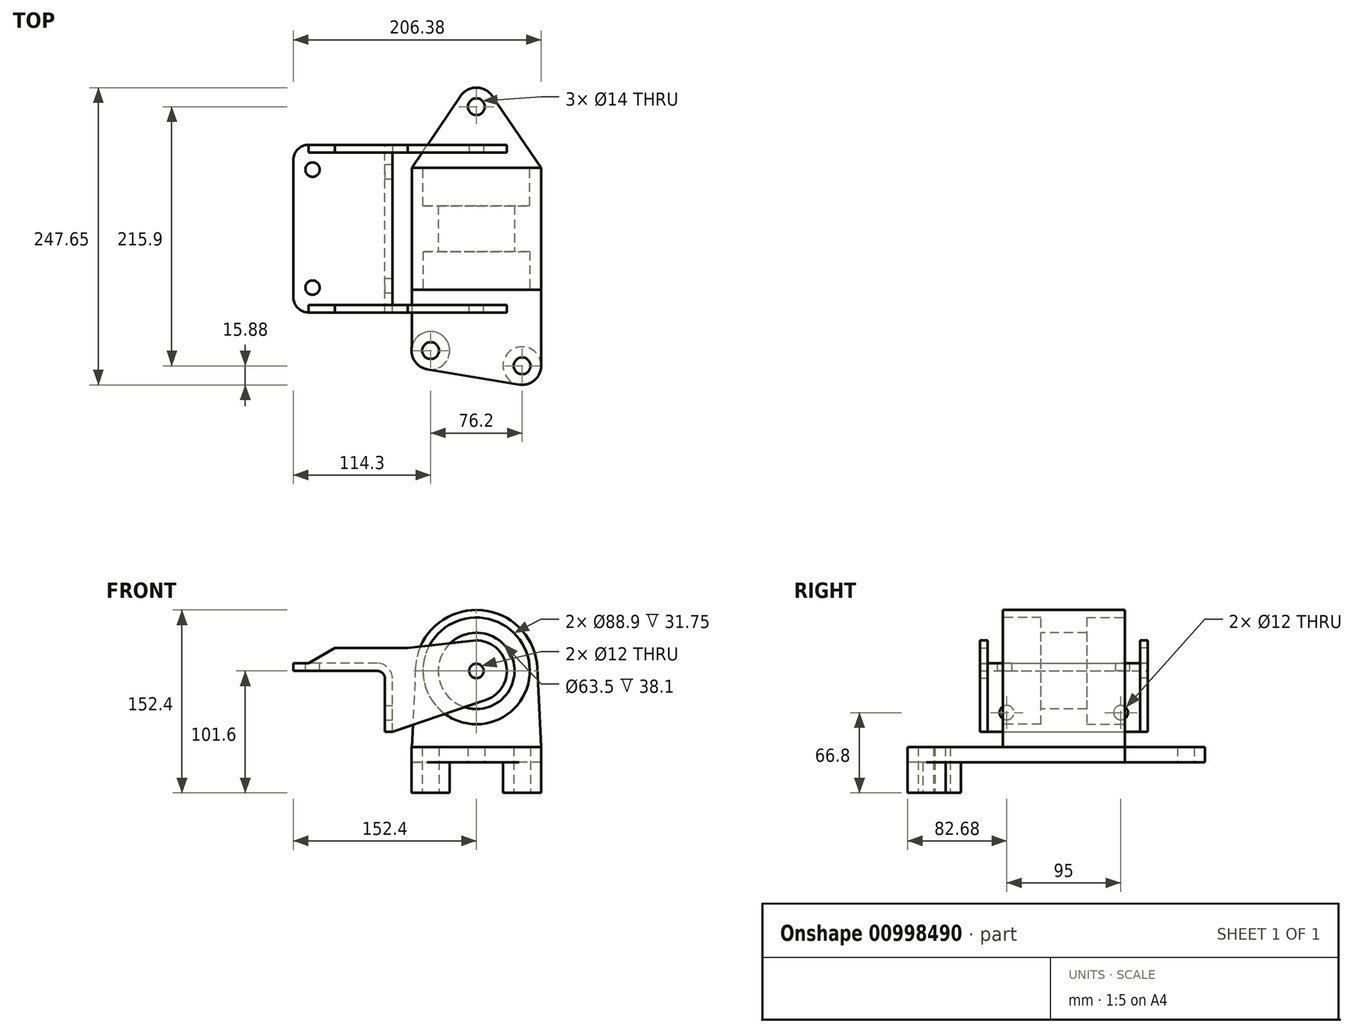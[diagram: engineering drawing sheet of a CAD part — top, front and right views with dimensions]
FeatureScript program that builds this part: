
annotation { "Feature Type Name" : "Feature", "Feature Type Description" : "" }
export const myFeature = defineFeature(function(context is Context, id is Id, definition is map)
    precondition{}
    {
        {
            var Q0;
            Q0=qCreatedBy(makeId("Top.planeOp"),FACE);
            var sketch = newSketch(context, id + "F0", { "sketchPlane" : qUnion([Q0])});
            skLineSegment(sketch, "E0", {"start": v(-38.1, -203.2) * mm, "end": v(0, 0) * mm});
            skLineSegment(sketch, "E1", {"start": v(0, 0) * mm, "end": v(38.1, -215.9) * mm});
            skSolve(sketch);
        }
        {
            var Q0;
            Q0=qCreatedBy(makeId("Top.planeOp"),FACE);
            var sketch = newSketch(context, id + "F1", { "sketchPlane" : qUnion([Q0])});
            skLineSegment(sketch, "E2.0", {"start": v(15.63, 2.76) * mm, "end": v(53.73, -213.14) * mm});
            skLineSegment(sketch, "E2.1", {"start": v(-53.7, -200.27) * mm, "end": v(-15.6, 2.93) * mm});
            skPoint(sketch, "E3.visualSharp", {"position": v(0.47, 88.67) * mm});
            skArc(sketch, "E3.filletArc", {"start": v(15.63, 2.76) * mm, "mid": v(0.08, 15.87) * mm, "end": v(-15.6, 2.93) * mm});
            skLineSegment(sketch, "E4", {"start": v(-53.7, -200.27) * mm, "end": v(-38.1, -203.2) * mm, "construction": true});
            skLineSegment(sketch, "E5", {"start": v(53.73, -213.14) * mm, "end": v(38.1, -215.9) * mm, "construction": true});
            skArc(sketch, "E6", {"start": v(-53.7, -200.27) * mm, "mid": v(-51.11, -212.3) * mm, "end": v(-40.7, -218.86) * mm});
            skPoint(sketch, "E6.endSnap0", {"position": v(-45.9, -201.74) * mm});
            skLineSegment(sketch, "E7", {"start": v(-40.7, -218.86) * mm, "end": v(35.5, -231.56) * mm});
            skArc(sketch, "E8", {"start": v(35.5, -231.56) * mm, "mid": v(49.38, -227.07) * mm, "end": v(53.73, -213.14) * mm});
            skCircle(sketch, "E9", {"center": v(0, 0) * mm, "radius": 7 * mm});
            skCircle(sketch, "E10", {"center": v(-38.1, -203.2) * mm, "radius": 7 * mm});
            skCircle(sketch, "E11", {"center": v(38.1, -215.9) * mm, "radius": 7 * mm});
            skSolve(sketch);
        }
        {
            var Q0;
            Q0 = qSketchRegion(id + "F1", true);
            extrude(context, id + "F2", {"entities" : qUnion([Q0]), "depth" : 12.7 * mm, "offsetDistance" : 25.4 * mm});
        }
        {
            var Q0;
            Q0=makeQuery(id+"F2.opExtrude","CAP_FACE",FACE,{"disambiguationData":[OSD([sQuery(id+"F1.wireOp",EDGE,"E2.0"),sQuery(id+"F1.wireOp",EDGE,"E2.1"),sQuery(id+"F1.wireOp",EDGE,"E3.filletArc"),sQuery(id+"F1.wireOp",EDGE,"E6"),sQuery(id+"F1.wireOp",EDGE,"E7"),sQuery(id+"F1.wireOp",EDGE,"E8"),sQuery(id+"F1.wireOp",EDGE,"E9"),sQuery(id+"F1.wireOp",EDGE,"E10"),sQuery(id+"F1.wireOp",EDGE,"E11")])],"isStart":true});
            var sketch = newSketch(context, id + "F3", { "sketchPlane" : qUnion([Q0])});
            skCircle(sketch, "E12", {"center": v(-38.1, 203.2) * mm, "radius": 15.87 * mm});
            skCircle(sketch, "E13.0", {"center": v(-38.1, 203.2) * mm, "radius": 7 * mm});
            skSolve(sketch);
        }
        {
            var Q0;
            Q0 = qSketchRegion(id + "F3", true);
            extrude(context, id + "F4", {"entities" : qUnion([Q0]), "operationType" : NewBodyOperationType.ADD, "depth" : 25.4 * mm, "offsetDistance" : 25.4 * mm});
        }
        {
            var Q0;
            Q0=makeQuery(id+"F2.opExtrude","CAP_FACE",FACE,{"disambiguationData":[OSD([sQuery(id+"F1.wireOp",EDGE,"E2.0"),sQuery(id+"F1.wireOp",EDGE,"E2.1"),sQuery(id+"F1.wireOp",EDGE,"E3.filletArc"),sQuery(id+"F1.wireOp",EDGE,"E6"),sQuery(id+"F1.wireOp",EDGE,"E7"),sQuery(id+"F1.wireOp",EDGE,"E8"),sQuery(id+"F1.wireOp",EDGE,"E9"),sQuery(id+"F1.wireOp",EDGE,"E10"),sQuery(id+"F1.wireOp",EDGE,"E11")])],"isStart":true});
            var sketch = newSketch(context, id + "F5", { "sketchPlane" : qUnion([Q0])});
            skCircle(sketch, "E14", {"center": v(38.1, 215.9) * mm, "radius": 15.88 * mm});
            skCircle(sketch, "E15.0", {"center": v(38.1, 215.9) * mm, "radius": 7 * mm});
            skSolve(sketch);
        }
        {
            var Q0;
            Q0 = qSketchRegion(id + "F5", true);
            extrude(context, id + "F6", {"entities" : qUnion([Q0]), "operationType" : NewBodyOperationType.ADD, "depth" : 25.4 * mm, "offsetDistance" : 25.4 * mm});
        }
        {
            var Q0;
            Q0=qCreatedBy(makeId("Front.planeOp"),FACE);
            cPlane(context, id + "F7", {"entities" : qUnion([Q0]), "cplaneType" : CPlaneType.OFFSET, "offset" : 101.6 * mm, "width" : 152.4 * mm, "height" : 152.4 * mm});
        }
        {
            var Q0;
            Q0=qCreatedBy(id+"F7.planeOp",FACE);
            var sketch = newSketch(context, id + "F8", { "sketchPlane" : qUnion([Q0])});
            skLineSegment(sketch, "E16.0.0", {"start": v(-53.98, 12.7) * mm, "end": v(-40.7, 12.7) * mm, "construction": true});
            skLineSegment(sketch, "E16.0.1", {"start": v(-40.7, 12.7) * mm, "end": v(35.5, 12.7) * mm, "construction": true});
            skLineSegment(sketch, "E16.0.2", {"start": v(35.5, 12.7) * mm, "end": v(53.97, 12.7) * mm, "construction": true});
            skLineSegment(sketch, "E16.0.3", {"start": v(53.73, 12.7) * mm, "end": v(15.63, 12.7) * mm, "construction": true});
            skLineSegment(sketch, "E16.0.4", {"start": v(15.63, 12.7) * mm, "end": v(-15.6, 12.7) * mm, "construction": true});
            skLineSegment(sketch, "E16.0.5", {"start": v(-15.6, 12.7) * mm, "end": v(-53.7, 12.7) * mm, "construction": true});
            skArc(sketch, "E17", {"start": v(50.74, 78.69) * mm, "mid": v(-0.1, 127) * mm, "end": v(-50.75, 78.48) * mm});
            skLineSegment(sketch, "E18", {"start": v(50.74, 78.69) * mm, "end": v(53.98, 12.7) * mm});
            skLineSegment(sketch, "E19", {"start": v(-50.75, 78.48) * mm, "end": v(-53.7, 12.7) * mm});
            skLineSegment(sketch, "E20", {"start": v(-53.7, 12.7) * mm, "end": v(53.97, 12.7) * mm});
            skSolve(sketch);
        }
        {
            var Q0;
            Q0 = qSketchRegion(id + "F8", true);
            extrude(context, id + "F9", {"entities" : qUnion([Q0]), "operationType" : NewBodyOperationType.ADD, "endBound" : BoundingType.SYMMETRIC, "depth" : 101.6 * mm, "offsetDistance" : 25.4 * mm});
        }
        {
            var Q0;
            Q0=makeQuery(id+"F9.opExtrude","CAP_FACE",FACE,{"disambiguationData":[OSD([sQuery(id+"F8.wireOp",EDGE,"E17"),sQuery(id+"F8.wireOp",EDGE,"E18"),sQuery(id+"F8.wireOp",EDGE,"E19"),sQuery(id+"F8.wireOp",EDGE,"E20")])],"isStart":false});
            var sketch = newSketch(context, id + "F10", { "sketchPlane" : qUnion([Q0])});
            skCircle(sketch, "E21", {"center": v(0, 76.2) * mm, "radius": 44.45 * mm});
            skSolve(sketch);
        }
        {
            var Q0;
            Q0 = qSketchRegion(id + "F10", true);
            extrude(context, id + "F11", {"entities" : qUnion([Q0]), "operationType" : NewBodyOperationType.REMOVE, "oppositeDirection" : true, "depth" : 31.75 * mm, "offsetDistance" : 25.4 * mm});
        }
        {
            var Q0;
            Q0=makeQuery(id+"F9.opExtrude","CAP_FACE",FACE,{"disambiguationData":[OSD([sQuery(id+"F8.wireOp",EDGE,"E17"),sQuery(id+"F8.wireOp",EDGE,"E18"),sQuery(id+"F8.wireOp",EDGE,"E19"),sQuery(id+"F8.wireOp",EDGE,"E20")])],"isStart":true});
            var sketch = newSketch(context, id + "F12", { "sketchPlane" : qUnion([Q0])});
            skCircle(sketch, "E22.0", {"center": v(0, 76.2) * mm, "radius": 44.45 * mm});
            skSolve(sketch);
        }
        {
            var Q0;
            Q0 = qSketchRegion(id + "F12", true);
            extrude(context, id + "F13", {"entities" : qUnion([Q0]), "operationType" : NewBodyOperationType.REMOVE, "oppositeDirection" : true, "depth" : 31.75 * mm, "offsetDistance" : 25.4 * mm});
        }
        {
            var Q0;
            Q0=makeQuery(id+"F11.boolean.opBoolean","COPY",FACE,{"derivedFrom":makeQuery(id+"F11.opExtrude","CAP_FACE",FACE,{"disambiguationData":[OSD([sQuery(id+"F10.wireOp",EDGE,"E21")])],"isStart":false})});
            var sketch = newSketch(context, id + "F14", { "sketchPlane" : qUnion([Q0])});
            skCircle(sketch, "E23", {"center": v(0, 76.2) * mm, "radius": 31.75 * mm});
            skSolve(sketch);
        }
        {
            var Q0;
            Q0 = qSketchRegion(id + "F14", true);
            extrude(context, id + "F15", {"entities" : qUnion([Q0]), "operationType" : NewBodyOperationType.REMOVE, "endBound" : BoundingType.THROUGH_ALL, "oppositeDirection" : true, "depth" : 25.4 * mm, "offsetDistance" : 25.4 * mm});
        }
        {
            var Q0;
            Q0=qCreatedBy(makeId("Front.planeOp"),FACE);
            var sketch = newSketch(context, id + "F16", { "sketchPlane" : qUnion([Q0])});
            skLineSegment(sketch, "E24", {"start": v(-76.2, 25.4) * mm, "end": v(-76.2, 76.2) * mm});
            skLineSegment(sketch, "E25", {"start": v(-76.2, 76.2) * mm, "end": v(-152.4, 76.2) * mm});
            skLineSegment(sketch, "E26.0", {"start": v(-69.85, 82.55) * mm, "end": v(-152.4, 82.55) * mm});
            skLineSegment(sketch, "E26.1", {"start": v(-69.85, 25.4) * mm, "end": v(-69.85, 82.55) * mm});
            skLineSegment(sketch, "E27", {"start": v(-152.4, 76.2) * mm, "end": v(-152.4, 82.55) * mm});
            skLineSegment(sketch, "E28", {"start": v(-76.2, 25.4) * mm, "end": v(-69.85, 25.4) * mm});
            skSolve(sketch);
        }
        {
            var Q0;
            Q0 = qSketchRegion(id + "F16", true);
            extrude(context, id + "F17", {"entities" : qUnion([Q0]), "depth" : 171.45 * mm, "offsetDistance" : 25.4 * mm, "hasSecondDirection" : true, "secondDirectionOppositeDirection" : false, "secondDirectionDepth" : 31.75 * mm});
        }
        {
            var Q0;
            Q0=makeQuery(id+"F17.opExtrude","SWEPT_FACE",FACE,{"disambiguationData":[OSD([sQuery(id+"F16.wireOp",EDGE,"E26.0")])]});
            var sketch = newSketch(context, id + "F18", { "sketchPlane" : qUnion([Q0])});
            skCircle(sketch, "E29", {"center": v(-136.4, -150.75) * mm, "radius": 6 * mm});
            skCircle(sketch, "E30", {"center": v(-136.4, -52.45) * mm, "radius": 6 * mm});
            skLineSegment(sketch, "E31", {"start": v(-136.4, -150.75) * mm, "end": v(-136.4, -52.45) * mm, "construction": true});
            skSolve(sketch);
        }
        {
            var Q0;
            Q0=makeQuery(id+"F17.opExtrude","SWEPT_FACE",FACE,{"disambiguationData":[OSD([sQuery(id+"F16.wireOp",EDGE,"E26.1")])]});
            var sketch = newSketch(context, id + "F19", { "sketchPlane" : qUnion([Q0])});
            skCircle(sketch, "E32", {"center": v(-54.1, 41.4) * mm, "radius": 6 * mm});
            skCircle(sketch, "E33", {"center": v(-149.1, 41.4) * mm, "radius": 6 * mm});
            skLineSegment(sketch, "E34", {"start": v(-54.1, 41.4) * mm, "end": v(-149.1, 41.4) * mm, "construction": true});
            skSolve(sketch);
        }
        {
            var Q0;
            Q0 = qSketchRegion(id + "F18", true);
            extrude(context, id + "F20", {"entities" : qUnion([Q0]), "operationType" : NewBodyOperationType.REMOVE, "endBound" : BoundingType.UP_TO_NEXT, "oppositeDirection" : true, "depth" : 25.4 * mm, "offsetDistance" : 25.4 * mm});
        }
        {
            var Q0;
            Q0 = qSketchRegion(id + "F19", true);
            extrude(context, id + "F21", {"entities" : qUnion([Q0]), "operationType" : NewBodyOperationType.REMOVE, "endBound" : BoundingType.UP_TO_NEXT, "oppositeDirection" : true, "depth" : 25.4 * mm, "offsetDistance" : 25.4 * mm});
        }
        {
            var Q0;
            Q0=makeQuery(id+"F17.opExtrude","SWEPT_EDGE",EDGE,{"disambiguationData":[OSD([sQuery(id+"F16.wireOp",EDGE,"E24"),sQuery(id+"F16.wireOp",EDGE,"E25")])]});
            fillet(context, id + "F22", {"entities" : qUnion([Q0]), "radius" : 6.35 * mm, "tangentPropagation" : true, "allowEdgeOverflow" : false});
        }
        {
            var Q0;
            Q0=makeQuery(id+"F17.opExtrude","SWEPT_EDGE",EDGE,{"disambiguationData":[OSD([sQuery(id+"F16.wireOp",EDGE,"E26.0"),sQuery(id+"F16.wireOp",EDGE,"E26.1")])]});
            fillet(context, id + "F23", {"entities" : qUnion([Q0]), "radius" : 12.7 * mm, "tangentPropagation" : true, "allowEdgeOverflow" : false});
        }
        {
            var Q0;
            Q0=makeQuery(id+"F9.opExtrude","CAP_FACE",FACE,{"disambiguationData":[OSD([sQuery(id+"F8.wireOp",EDGE,"E17"),sQuery(id+"F8.wireOp",EDGE,"E18"),sQuery(id+"F8.wireOp",EDGE,"E19"),sQuery(id+"F8.wireOp",EDGE,"E20")])],"isStart":false});
            var sketch = newSketch(context, id + "F24", { "sketchPlane" : qUnion([Q0])});
            skLineSegment(sketch, "E35", {"start": v(-139.7, 82.55) * mm, "end": v(-117.7, 95.25) * mm});
            skLineSegment(sketch, "E36", {"start": v(-117.7, 95.25) * mm, "end": v(-57.15, 95.25) * mm});
            skLineSegment(sketch, "E37", {"start": v(-57.15, 95.25) * mm, "end": v(-2.88, 101.44) * mm});
            skArc(sketch, "E38", {"start": v(8.24, 52.17) * mm, "mid": v(24.78, 81.8) * mm, "end": v(-2.88, 101.44) * mm});
            skLineSegment(sketch, "E39", {"start": v(-69.85, 25.4) * mm, "end": v(8.24, 52.17) * mm});
            skLineSegment(sketch, "E40.0", {"start": v(-82.55, 82.55) * mm, "end": v(-139.7, 82.55) * mm});
            skArc(sketch, "E40.1", {"start": v(-69.85, 69.85) * mm, "mid": v(-73.57, 78.83) * mm, "end": v(-82.55, 82.55) * mm});
            skCircle(sketch, "E41", {"center": v(0, 76.2) * mm, "radius": 6 * mm});
            skLineSegment(sketch, "E42.0", {"start": v(-69.85, 25.4) * mm, "end": v(-69.85, 69.85) * mm});
            skSolve(sketch);
        }
        {
            var Q0;
            Q0 = qSketchRegion(id + "F24", true);
            extrude(context, id + "F25", {"entities" : qUnion([Q0]), "operationType" : NewBodyOperationType.ADD, "depth" : 19.05 * mm, "offsetDistance" : 25.4 * mm, "hasSecondDirection" : true, "secondDirectionOppositeDirection" : false, "secondDirectionDepth" : 12.7 * mm});
        }
        {
            var Q0;
            Q0=makeQuery(id+"F9.opExtrude","CAP_FACE",FACE,{"disambiguationData":[OSD([sQuery(id+"F8.wireOp",EDGE,"E17"),sQuery(id+"F8.wireOp",EDGE,"E18"),sQuery(id+"F8.wireOp",EDGE,"E19"),sQuery(id+"F8.wireOp",EDGE,"E20")])],"isStart":true});
            var sketch = newSketch(context, id + "F26", { "sketchPlane" : qUnion([Q0])});
            skLineSegment(sketch, "E43.0", {"start": v(139.7, 82.55) * mm, "end": v(117.7, 95.25) * mm});
            skLineSegment(sketch, "E43.1", {"start": v(117.7, 95.25) * mm, "end": v(57.15, 95.25) * mm});
            skLineSegment(sketch, "E43.2", {"start": v(57.15, 95.25) * mm, "end": v(2.88, 101.44) * mm});
            skArc(sketch, "E43.3", {"start": v(-8.24, 52.17) * mm, "mid": v(-24.78, 81.8) * mm, "end": v(2.88, 101.44) * mm});
            skLineSegment(sketch, "E43.4", {"start": v(69.85, 25.4) * mm, "end": v(-8.24, 52.17) * mm});
            skLineSegment(sketch, "E43.5", {"start": v(82.55, 82.55) * mm, "end": v(139.7, 82.55) * mm});
            skArc(sketch, "E43.6", {"start": v(69.85, 69.85) * mm, "mid": v(73.57, 78.83) * mm, "end": v(82.55, 82.55) * mm});
            skCircle(sketch, "E43.7", {"center": v(0, 76.2) * mm, "radius": 6 * mm});
            skLineSegment(sketch, "E43.8", {"start": v(69.85, 25.4) * mm, "end": v(69.85, 69.85) * mm});
            skSolve(sketch);
        }
        {
            var Q0;
            Q0 = qSketchRegion(id + "F26", true);
            extrude(context, id + "F27", {"entities" : qUnion([Q0]), "operationType" : NewBodyOperationType.ADD, "depth" : 19.05 * mm, "offsetDistance" : 25.4 * mm, "hasSecondDirection" : true, "secondDirectionOppositeDirection" : false, "secondDirectionDepth" : 12.7 * mm});
        }
        {
            var Q0;
            Q0=makeQuery(id+"F2.opExtrude","CAP_FACE",FACE,{"disambiguationData":[OSD([sQuery(id+"F1.wireOp",EDGE,"E2.0"),sQuery(id+"F1.wireOp",EDGE,"E2.1"),sQuery(id+"F1.wireOp",EDGE,"E3.filletArc"),sQuery(id+"F1.wireOp",EDGE,"E6"),sQuery(id+"F1.wireOp",EDGE,"E7"),sQuery(id+"F1.wireOp",EDGE,"E8"),sQuery(id+"F1.wireOp",EDGE,"E9"),sQuery(id+"F1.wireOp",EDGE,"E10"),sQuery(id+"F1.wireOp",EDGE,"E11")])],"isStart":true});
            var sketch = newSketch(context, id + "F28", { "sketchPlane" : qUnion([Q0])});
            skLineSegment(sketch, "E44.0.0", {"start": v(-25.68, 50.8) * mm, "end": v(-44.73, 152.4) * mm});
            skLineSegment(sketch, "E44.0.1", {"start": v(-44.73, 152.4) * mm, "end": v(-53.7, 152.4) * mm});
            skLineSegment(sketch, "E44.0.2", {"start": v(-53.7, 152.4) * mm, "end": v(-53.7, 50.8) * mm});
            skLineSegment(sketch, "E44.0.3", {"start": v(-53.7, 50.8) * mm, "end": v(-25.68, 50.8) * mm});
            skLineSegment(sketch, "E44.1.0", {"start": v(43.01, 152.4) * mm, "end": v(25.08, 50.8) * mm});
            skLineSegment(sketch, "E44.1.1", {"start": v(25.08, 50.8) * mm, "end": v(53.97, 50.8) * mm});
            skLineSegment(sketch, "E44.1.2", {"start": v(53.97, 50.8) * mm, "end": v(53.97, 152.4) * mm});
            skLineSegment(sketch, "E44.1.3", {"start": v(53.97, 152.4) * mm, "end": v(43.01, 152.4) * mm});
            skLineSegment(sketch, "E45", {"start": v(-53.7, 152.4) * mm, "end": v(-53.7, 200.27) * mm});
            skLineSegment(sketch, "E46", {"start": v(53.97, 152.4) * mm, "end": v(53.97, 215.9) * mm});
            skLineSegment(sketch, "E47", {"start": v(-53.7, 50.8) * mm, "end": v(-13.13, -8.92) * mm});
            skLineSegment(sketch, "E48", {"start": v(53.97, 50.8) * mm, "end": v(13.1, -8.96) * mm});
            skArc(sketch, "E49.0", {"start": v(53.73, 213.14) * mm, "mid": v(53.91, 214.52) * mm, "end": v(53.98, 215.9) * mm});
            skLineSegment(sketch, "E49.1", {"start": v(15.63, -2.76) * mm, "end": v(53.73, 213.14) * mm});
            skSolve(sketch);
        }
        {
            var Q0;
            {var subQ0=sQuery(id+"F28.wireOp",EDGE,"E44.0.1");Q0=makeQuery(id+"F28.imprint","IMPRINT",FACE,{"disambiguationData":[TD([[makeQuery(id+"F28.imprint","IMPRINT",EDGE,{"derivedFrom":subQ0}),-1.0]])]});}
            var Q1;
            Q1=makeQuery(id+"F28.imprint","IMPRINT",FACE,{"disambiguationData":[TD([[makeQuery(id+"F28.imprint","IMPRINT",EDGE,{"derivedFrom":sQuery(id+"F28.wireOp",EDGE,"E44.0.0")}),-1.0]])]});
            var Q2;
            {var subQ0=sQuery(id+"F28.wireOp",EDGE,"E44.0.3");Q2=makeQuery(id+"F28.imprint","IMPRINT",FACE,{"disambiguationData":[TD([[makeQuery(id+"F28.imprint","IMPRINT",EDGE,{"derivedFrom":subQ0}),-1.0]])]});}
            var Q3;
            {var subQ0=sQuery(id+"F28.wireOp",EDGE,"E44.1.1");Q3=makeQuery(id+"F28.imprint","IMPRINT",FACE,{"disambiguationData":[TD([[makeQuery(id+"F28.imprint","IMPRINT",EDGE,{"derivedFrom":subQ0}),-1.0]])]});}
            var Q4;
            Q4=makeQuery(id+"F28.imprint","IMPRINT",FACE,{"disambiguationData":[TD([[makeQuery(id+"F28.imprint","IMPRINT",EDGE,{"derivedFrom":sQuery(id+"F28.wireOp",EDGE,"E44.1.0")}),-1.0]])]});
            var Q5;
            {var subQ0=sQuery(id+"F28.wireOp",EDGE,"E44.1.3");Q5=makeQuery(id+"F28.imprint","IMPRINT",FACE,{"disambiguationData":[TD([[makeQuery(id+"F28.imprint","IMPRINT",EDGE,{"derivedFrom":subQ0}),-1.0]])]});}
            extrude(context, id + "F29", {"entities" : qUnion([Q0, Q1, Q2, Q3, Q4, Q5]), "operationType" : NewBodyOperationType.ADD, "oppositeDirection" : true, "depth" : 12.7 * mm, "offsetDistance" : 25.4 * mm});
        }
        {
            var Q0;
            Q0=makeQuery(id+"F17.opExtrude","CAP_EDGE",EDGE,{"disambiguationData":[OSD([sQuery(id+"F16.wireOp",EDGE,"E27")])],"isStart":false});
            var Q1;
            Q1=makeQuery(id+"F17.opExtrude","CAP_EDGE",EDGE,{"disambiguationData":[OSD([sQuery(id+"F16.wireOp",EDGE,"E27")])],"isStart":true});
            fillet(context, id + "F30", {"entities" : qUnion([Q0, Q1]), "radius" : 12.7 * mm, "tangentPropagation" : true, "allowEdgeOverflow" : false});
        }
    });
